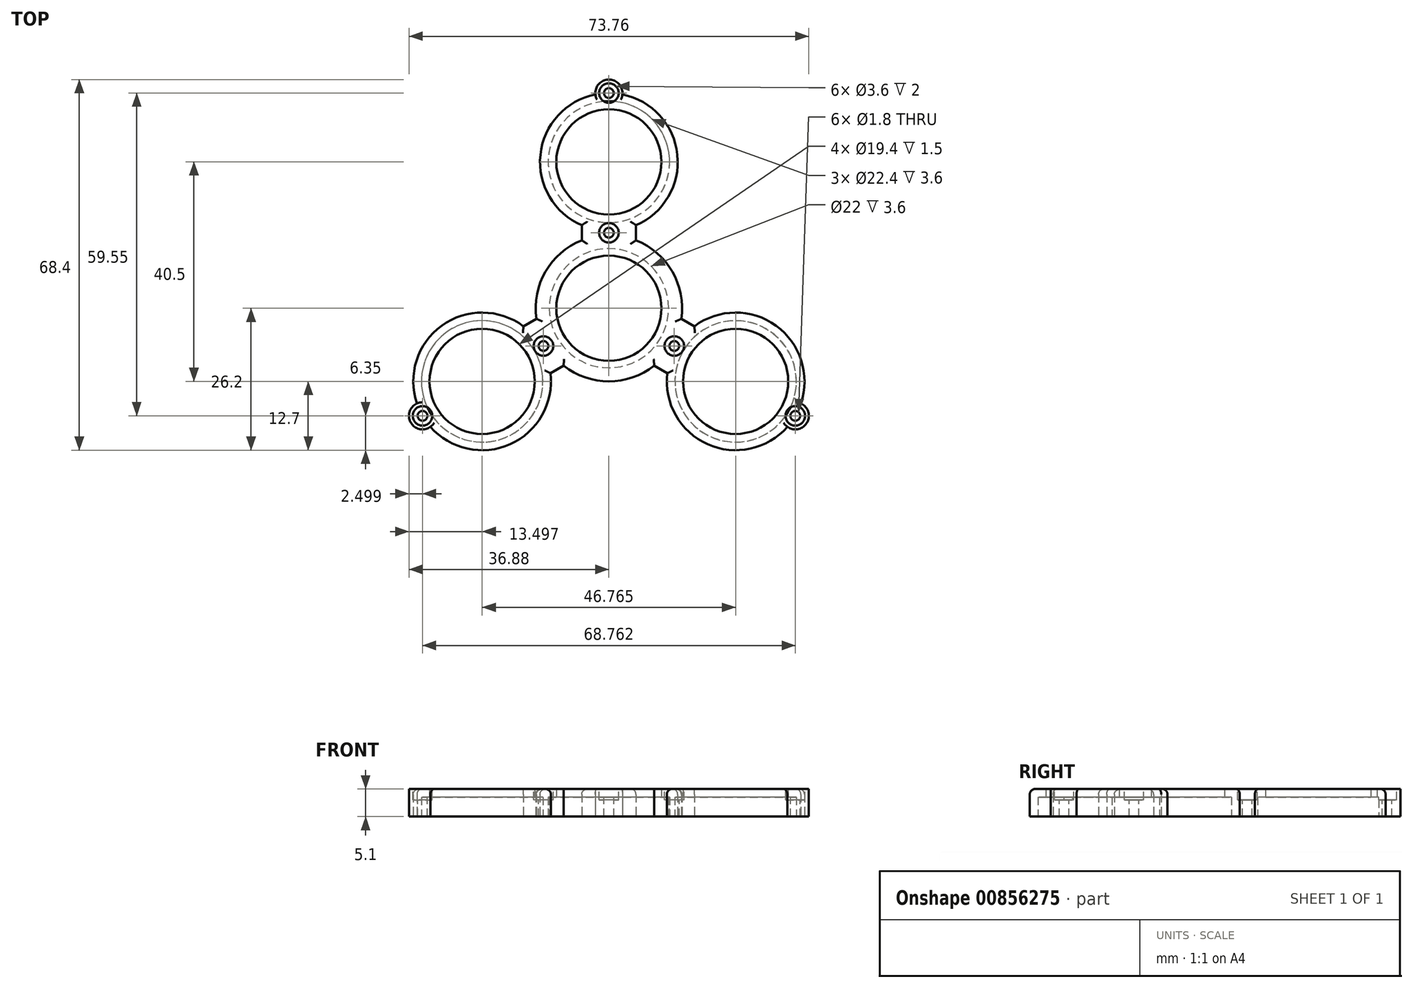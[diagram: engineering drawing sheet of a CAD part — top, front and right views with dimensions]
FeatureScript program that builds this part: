
annotation { "Feature Type Name" : "Feature", "Feature Type Description" : "" }
export const myFeature = defineFeature(function(context is Context, id is Id, definition is map)
    precondition{}
    {
        {
            var Q0;
            Q0=qCreatedBy(makeId("Top.planeOp"),FACE);
            var sketch = newSketch(context, id + "F0", { "sketchPlane" : qUnion([Q0])});
            skCircle(sketch, "E0", {"center": v(0, 0) * mm, "radius": 11 * mm});
            skCircle(sketch, "E1", {"center": v(0, 27) * mm, "radius": 11.2 * mm});
            skLineSegment(sketch, "E2", {"start": v(-5, 15.33) * mm, "end": v(-5, 12.54) * mm});
            skLineSegment(sketch, "E3", {"start": v(5, 15.33) * mm, "end": v(5, 12.54) * mm});
            skLineSegment(sketch, "E4", {"start": v(0, 27) * mm, "end": v(0, 13.5) * mm, "construction": true});
            skLineSegment(sketch, "E5", {"start": v(-5, 13.93) * mm, "end": v(0, 13.93) * mm, "construction": true});
            skLineSegment(sketch, "E6", {"start": v(0, 13.5) * mm, "end": v(0, 0) * mm, "construction": true});
            skLineSegment(sketch, "E7", {"start": v(0, 13.93) * mm, "end": v(5, 13.93) * mm, "construction": true});
            skArc(sketch, "E8", {"start": v(-2.49, 39.45) * mm, "mid": v(0, 37.2) * mm, "end": v(2.49, 39.45) * mm, "construction": true});
            skArc(sketch, "E9", {"start": v(2.49, 39.45) * mm, "mid": v(0, 42.2) * mm, "end": v(-2.49, 39.45) * mm});
            skArc(sketch, "E10", {"start": v(-2.49, 39.45) * mm, "mid": v(-12.63, 28.32) * mm, "end": v(-5, 15.33) * mm});
            skArc(sketch, "E11", {"start": v(-5, 15.33) * mm, "mid": v(0, 14.3) * mm, "end": v(5, 15.33) * mm, "construction": true});
            skArc(sketch, "E12", {"start": v(5, 15.33) * mm, "mid": v(12.63, 28.32) * mm, "end": v(2.49, 39.45) * mm});
            skArc(sketch, "E13", {"start": v(-5, 12.54) * mm, "mid": v(0, -13.5) * mm, "end": v(5, 12.54) * mm});
            skArc(sketch, "E14", {"start": v(5, 12.54) * mm, "mid": v(0, 13.5) * mm, "end": v(-5, 12.54) * mm, "construction": true});
            skArc(sketch, "E15.1.0", {"start": v(-35.41, -17.57) * mm, "mid": v(-36.55, -21.1) * mm, "end": v(-32.92, -21.88) * mm});
            skArc(sketch, "E15.1.1", {"start": v(-32.92, -21.88) * mm, "mid": v(-18.2, -25.1) * mm, "end": v(-10.77, -12) * mm});
            skLineSegment(sketch, "E15.1.2", {"start": v(-10.77, -12) * mm, "end": v(-8.36, -10.6) * mm});
            skArc(sketch, "E15.1.3", {"start": v(-15.77, -3.33) * mm, "mid": v(-30.84, -3.22) * mm, "end": v(-35.41, -17.57) * mm});
            skLineSegment(sketch, "E15.1.4", {"start": v(-15.77, -3.33) * mm, "end": v(-13.36, -1.94) * mm});
            skCircle(sketch, "E15.1.5", {"center": v(-23.38, -13.5) * mm, "radius": 11.2 * mm});
            skArc(sketch, "E15.2.0", {"start": v(32.92, -21.88) * mm, "mid": v(36.55, -21.1) * mm, "end": v(35.41, -17.57) * mm});
            skArc(sketch, "E15.2.1", {"start": v(35.41, -17.57) * mm, "mid": v(30.84, -3.22) * mm, "end": v(15.77, -3.33) * mm});
            skLineSegment(sketch, "E15.2.2", {"start": v(15.77, -3.33) * mm, "end": v(13.36, -1.94) * mm});
            skArc(sketch, "E15.2.3", {"start": v(10.77, -12) * mm, "mid": v(18.2, -25.1) * mm, "end": v(32.92, -21.88) * mm});
            skLineSegment(sketch, "E15.2.4", {"start": v(10.77, -12) * mm, "end": v(8.36, -10.6) * mm});
            skCircle(sketch, "E15.2.5", {"center": v(23.38, -13.5) * mm, "radius": 11.2 * mm});
            skSolve(sketch);
        }
        {
            var Q0;
            Q0=makeQuery(id+"F0.imprint","IMPRINT",FACE,{"disambiguationData":[TD([[makeQuery(id+"F0.imprint","IMPRINT",EDGE,{"derivedFrom":sQuery(id+"F0.wireOp",EDGE,"E0")}),-1.0]])]});
            var Q1;
            Q1=makeQuery(id+"F0.imprint","IMPRINT",FACE,{"disambiguationData":[TD([[makeQuery(id+"F0.imprint","IMPRINT",EDGE,{"derivedFrom":sQuery(id+"F0.wireOp",EDGE,"E15.1.0")}),1.0]])]});
            var Q2;
            Q2=makeQuery(id+"F0.imprint","IMPRINT",FACE,{"disambiguationData":[TD([[makeQuery(id+"F0.imprint","IMPRINT",EDGE,{"derivedFrom":sQuery(id+"F0.wireOp",EDGE,"E15.2.0")}),1.0]])]});
            extrude(context, id + "F1", {"entities" : qUnion([Q0, Q1, Q2]), "depth" : 3.6 * mm, "offsetDistance" : 25 * mm});
        }
        {
            var Q0;
            Q0=makeQuery(id+"F1.opExtrude","CAP_FACE",FACE,{"disambiguationData":[OSD([sQuery(id+"F0.wireOp",EDGE,"E0"),sQuery(id+"F0.wireOp",EDGE,"E1"),sQuery(id+"F0.wireOp",EDGE,"E2"),sQuery(id+"F0.wireOp",EDGE,"E3"),sQuery(id+"F0.wireOp",EDGE,"E9"),sQuery(id+"F0.wireOp",EDGE,"E10"),sQuery(id+"F0.wireOp",EDGE,"E12"),sQuery(id+"F0.wireOp",EDGE,"E13"),sQuery(id+"F0.wireOp",EDGE,"E15.1.0"),sQuery(id+"F0.wireOp",EDGE,"E15.1.1"),sQuery(id+"F0.wireOp",EDGE,"E15.1.2"),sQuery(id+"F0.wireOp",EDGE,"E15.1.3"),sQuery(id+"F0.wireOp",EDGE,"E15.1.4"),sQuery(id+"F0.wireOp",EDGE,"E15.1.5"),sQuery(id+"F0.wireOp",EDGE,"E15.2.0"),sQuery(id+"F0.wireOp",EDGE,"E15.2.1"),sQuery(id+"F0.wireOp",EDGE,"E15.2.2"),sQuery(id+"F0.wireOp",EDGE,"E15.2.3"),sQuery(id+"F0.wireOp",EDGE,"E15.2.4"),sQuery(id+"F0.wireOp",EDGE,"E15.2.5")])],"isStart":false});
            var sketch = newSketch(context, id + "F2", { "sketchPlane" : qUnion([Q0])});
            skCircle(sketch, "E16", {"center": v(0, 0) * mm, "radius": 9.7 * mm});
            skCircle(sketch, "E17", {"center": v(0, 27) * mm, "radius": 9.7 * mm});
            skCircle(sketch, "E18.1.0", {"center": v(-23.38, -13.5) * mm, "radius": 9.7 * mm});
            skCircle(sketch, "E18.2.0", {"center": v(23.38, -13.5) * mm, "radius": 9.7 * mm});
            skSolve(sketch);
        }
        {
            var Q0;
            Q0=makeQuery(id+"F2.imprint","IMPRINT",FACE,{"disambiguationData":[TD([[makeQuery(id+"F2.imprint","IMPRINT",EDGE,{"derivedFrom":sQuery(id+"F2.wireOp",EDGE,"E17")}),-1.0]])]});
            var Q1;
            Q1=makeQuery(id+"F2.imprint","IMPRINT",FACE,{"disambiguationData":[TD([[makeQuery(id+"F2.imprint","IMPRINT",EDGE,{"derivedFrom":makeQuery(id+"F1.opExtrude","CAP_EDGE",EDGE,{"disambiguationData":[OSD([sQuery(id+"F0.wireOp",EDGE,"E0")])],"isStart":false})}),-1.0]])]});
            var Q2;
            Q2=makeQuery(id+"F2.imprint","IMPRINT",FACE,{"disambiguationData":[TD([[makeQuery(id+"F2.imprint","IMPRINT",EDGE,{"derivedFrom":sQuery(id+"F2.wireOp",EDGE,"E18.1.0")}),-1.0]])]});
            var Q3;
            Q3=makeQuery(id+"F2.imprint","IMPRINT",FACE,{"disambiguationData":[TD([[makeQuery(id+"F2.imprint","IMPRINT",EDGE,{"derivedFrom":sQuery(id+"F2.wireOp",EDGE,"E18.2.0")}),-1.0]])]});
            var Q4;
            Q4=makeQuery(id+"F2.imprint","IMPRINT",FACE,{"disambiguationData":[TD([[makeQuery(id+"F2.imprint","IMPRINT",EDGE,{"derivedFrom":sQuery(id+"F2.wireOp",EDGE,"E16")}),-1.0]])]});
            extrude(context, id + "F3", {"entities" : qUnion([Q0, Q1, Q2, Q3, Q4]), "operationType" : NewBodyOperationType.ADD, "depth" : 1.5 * mm, "offsetDistance" : 25 * mm});
        }
        {
            var Q0;
            Q0=makeQuery(id+"F3.opExtrude","CAP_FACE",FACE,{"disambiguationData":[OSD([sQuery(id+"F0.wireOp",EDGE,"E0"),sQuery(id+"F0.wireOp",EDGE,"E2"),sQuery(id+"F0.wireOp",EDGE,"E3"),sQuery(id+"F0.wireOp",EDGE,"E9"),sQuery(id+"F0.wireOp",EDGE,"E10"),sQuery(id+"F0.wireOp",EDGE,"E12"),sQuery(id+"F0.wireOp",EDGE,"E13"),sQuery(id+"F0.wireOp",EDGE,"E15.1.0"),sQuery(id+"F0.wireOp",EDGE,"E15.1.1"),sQuery(id+"F0.wireOp",EDGE,"E15.1.2"),sQuery(id+"F0.wireOp",EDGE,"E15.1.3"),sQuery(id+"F0.wireOp",EDGE,"E15.1.4"),sQuery(id+"F0.wireOp",EDGE,"E15.2.0"),sQuery(id+"F0.wireOp",EDGE,"E15.2.1"),sQuery(id+"F0.wireOp",EDGE,"E15.2.2"),sQuery(id+"F0.wireOp",EDGE,"E15.2.3"),sQuery(id+"F0.wireOp",EDGE,"E15.2.4"),sQuery(id+"F2.wireOp",EDGE,"E17"),sQuery(id+"F2.wireOp",EDGE,"E18.1.0"),sQuery(id+"F2.wireOp",EDGE,"E18.2.0")])],"isStart":false});
            var sketch = newSketch(context, id + "F4", { "sketchPlane" : qUnion([Q0])});
            skCircle(sketch, "E19", {"center": v(0, 39.7) * mm, "radius": 1.8 * mm});
            skCircle(sketch, "E20", {"center": v(0, 13.93) * mm, "radius": 1.8 * mm});
            skPoint(sketch, "E20.centerSnap0", {"position": v(-5, 13.93) * mm});
            skCircle(sketch, "E21.1.0", {"center": v(-34.38, -19.85) * mm, "radius": 1.8 * mm});
            skCircle(sketch, "E21.1.1", {"center": v(-12.07, -6.97) * mm, "radius": 1.8 * mm});
            skCircle(sketch, "E21.2.0", {"center": v(34.38, -19.85) * mm, "radius": 1.8 * mm});
            skCircle(sketch, "E21.2.1", {"center": v(12.07, -6.97) * mm, "radius": 1.8 * mm});
            skPoint(sketch, "E21.center", {"position": v(0, 0) * mm});
            skSolve(sketch);
        }
        {
            var Q0;
            Q0=makeQuery(id+"F4.imprint","IMPRINT",FACE,{"disambiguationData":[TD([[makeQuery(id+"F4.imprint","IMPRINT",EDGE,{"derivedFrom":sQuery(id+"F4.wireOp",EDGE,"E19")}),1.0]])]});
            var Q1;
            Q1=makeQuery(id+"F4.imprint","IMPRINT",FACE,{"disambiguationData":[TD([[makeQuery(id+"F4.imprint","IMPRINT",EDGE,{"derivedFrom":sQuery(id+"F4.wireOp",EDGE,"E20")}),1.0]])]});
            var Q2;
            Q2=makeQuery(id+"F4.imprint","IMPRINT",FACE,{"disambiguationData":[TD([[makeQuery(id+"F4.imprint","IMPRINT",EDGE,{"derivedFrom":sQuery(id+"F4.wireOp",EDGE,"E21.1.1")}),1.0]])]});
            var Q3;
            Q3=makeQuery(id+"F4.imprint","IMPRINT",FACE,{"disambiguationData":[TD([[makeQuery(id+"F4.imprint","IMPRINT",EDGE,{"derivedFrom":sQuery(id+"F4.wireOp",EDGE,"E21.1.0")}),1.0]])]});
            var Q4;
            Q4=makeQuery(id+"F4.imprint","IMPRINT",FACE,{"disambiguationData":[TD([[makeQuery(id+"F4.imprint","IMPRINT",EDGE,{"derivedFrom":sQuery(id+"F4.wireOp",EDGE,"E21.2.1")}),1.0]])]});
            var Q5;
            Q5=makeQuery(id+"F4.imprint","IMPRINT",FACE,{"disambiguationData":[TD([[makeQuery(id+"F4.imprint","IMPRINT",EDGE,{"derivedFrom":sQuery(id+"F4.wireOp",EDGE,"E21.2.0")}),1.0]])]});
            extrude(context, id + "F5", {"entities" : qUnion([Q0, Q1, Q2, Q3, Q4, Q5]), "operationType" : NewBodyOperationType.REMOVE, "oppositeDirection" : true, "depth" : 2 * mm, "offsetDistance" : 25 * mm});
        }
        {
            var Q0;
            Q0=makeQuery(id+"F3.opExtrude","CAP_FACE",FACE,{"disambiguationData":[OSD([sQuery(id+"F0.wireOp",EDGE,"E2"),sQuery(id+"F0.wireOp",EDGE,"E3"),sQuery(id+"F0.wireOp",EDGE,"E9"),sQuery(id+"F0.wireOp",EDGE,"E10"),sQuery(id+"F0.wireOp",EDGE,"E12"),sQuery(id+"F0.wireOp",EDGE,"E13"),sQuery(id+"F0.wireOp",EDGE,"E15.1.0"),sQuery(id+"F0.wireOp",EDGE,"E15.1.1"),sQuery(id+"F0.wireOp",EDGE,"E15.1.2"),sQuery(id+"F0.wireOp",EDGE,"E15.1.3"),sQuery(id+"F0.wireOp",EDGE,"E15.1.4"),sQuery(id+"F0.wireOp",EDGE,"E15.2.0"),sQuery(id+"F0.wireOp",EDGE,"E15.2.1"),sQuery(id+"F0.wireOp",EDGE,"E15.2.2"),sQuery(id+"F0.wireOp",EDGE,"E15.2.3"),sQuery(id+"F0.wireOp",EDGE,"E15.2.4"),sQuery(id+"F2.wireOp",EDGE,"E16"),sQuery(id+"F2.wireOp",EDGE,"E17"),sQuery(id+"F2.wireOp",EDGE,"E18.1.0"),sQuery(id+"F2.wireOp",EDGE,"E18.2.0")])],"isStart":false});
            var sketch = newSketch(context, id + "F6", { "sketchPlane" : qUnion([Q0])});
            skCircle(sketch, "E22", {"center": v(0, 39.7) * mm, "radius": 0.9 * mm});
            skCircle(sketch, "E23", {"center": v(0, 13.93) * mm, "radius": 0.9 * mm});
            skCircle(sketch, "E24.1.0", {"center": v(-34.38, -19.85) * mm, "radius": 0.9 * mm});
            skCircle(sketch, "E24.1.1", {"center": v(-12.07, -6.97) * mm, "radius": 0.9 * mm});
            skCircle(sketch, "E24.2.0", {"center": v(34.38, -19.85) * mm, "radius": 0.9 * mm});
            skCircle(sketch, "E24.2.1", {"center": v(12.07, -6.97) * mm, "radius": 0.9 * mm});
            skPoint(sketch, "E24.center", {"position": v(0, 0) * mm});
            skSolve(sketch);
        }
        {
            var Q0;
            Q0=makeQuery(id+"F6.imprint","IMPRINT",FACE,{"disambiguationData":[TD([[makeQuery(id+"F6.imprint","IMPRINT",EDGE,{"derivedFrom":sQuery(id+"F6.wireOp",EDGE,"E22")}),1.0]])]});
            var Q1;
            Q1=makeQuery(id+"F6.imprint","IMPRINT",FACE,{"disambiguationData":[TD([[makeQuery(id+"F6.imprint","IMPRINT",EDGE,{"derivedFrom":sQuery(id+"F6.wireOp",EDGE,"E23")}),1.0]])]});
            var Q2;
            Q2=makeQuery(id+"F6.imprint","IMPRINT",FACE,{"disambiguationData":[TD([[makeQuery(id+"F6.imprint","IMPRINT",EDGE,{"derivedFrom":sQuery(id+"F6.wireOp",EDGE,"E24.1.1")}),1.0]])]});
            var Q3;
            Q3=makeQuery(id+"F6.imprint","IMPRINT",FACE,{"disambiguationData":[TD([[makeQuery(id+"F6.imprint","IMPRINT",EDGE,{"derivedFrom":sQuery(id+"F6.wireOp",EDGE,"E24.1.0")}),1.0]])]});
            var Q4;
            Q4=makeQuery(id+"F6.imprint","IMPRINT",FACE,{"disambiguationData":[TD([[makeQuery(id+"F6.imprint","IMPRINT",EDGE,{"derivedFrom":sQuery(id+"F6.wireOp",EDGE,"E24.2.1")}),1.0]])]});
            var Q5;
            Q5=makeQuery(id+"F6.imprint","IMPRINT",FACE,{"disambiguationData":[TD([[makeQuery(id+"F6.imprint","IMPRINT",EDGE,{"derivedFrom":sQuery(id+"F6.wireOp",EDGE,"E24.2.0")}),1.0]])]});
            var Q6;
            Q6=makeQuery(id+"F1.opExtrude","CAP_FACE",FACE,{"disambiguationData":[OSD([sQuery(id+"F0.wireOp",EDGE,"E0"),sQuery(id+"F0.wireOp",EDGE,"E1"),sQuery(id+"F0.wireOp",EDGE,"E2"),sQuery(id+"F0.wireOp",EDGE,"E3"),sQuery(id+"F0.wireOp",EDGE,"E9"),sQuery(id+"F0.wireOp",EDGE,"E10"),sQuery(id+"F0.wireOp",EDGE,"E12"),sQuery(id+"F0.wireOp",EDGE,"E13"),sQuery(id+"F0.wireOp",EDGE,"E15.1.0"),sQuery(id+"F0.wireOp",EDGE,"E15.1.1"),sQuery(id+"F0.wireOp",EDGE,"E15.1.2"),sQuery(id+"F0.wireOp",EDGE,"E15.1.3"),sQuery(id+"F0.wireOp",EDGE,"E15.1.4"),sQuery(id+"F0.wireOp",EDGE,"E15.1.5"),sQuery(id+"F0.wireOp",EDGE,"E15.2.0"),sQuery(id+"F0.wireOp",EDGE,"E15.2.1"),sQuery(id+"F0.wireOp",EDGE,"E15.2.2"),sQuery(id+"F0.wireOp",EDGE,"E15.2.3"),sQuery(id+"F0.wireOp",EDGE,"E15.2.4"),sQuery(id+"F0.wireOp",EDGE,"E15.2.5")])],"isStart":true});
            extrude(context, id + "F7", {"entities" : qUnion([Q0, Q1, Q2, Q3, Q4, Q5]), "operationType" : NewBodyOperationType.REMOVE, "endBound" : BoundingType.UP_TO_SURFACE, "oppositeDirection" : true, "depth" : 25 * mm, "endBoundEntityFace" : qUnion([Q6]), "offsetDistance" : 25 * mm});
        }
        {
            var Q0;
            Q0=makeQuery(id+"F3.opExtrude","CAP_EDGE",EDGE,{"disambiguationData":[OSD([sQuery(id+"F0.wireOp",EDGE,"E15.1.1")])],"isStart":false});
            var Q1;
            Q1=makeQuery(id+"F3.opExtrude","CAP_EDGE",EDGE,{"disambiguationData":[OSD([sQuery(id+"F0.wireOp",EDGE,"E15.1.2")])],"isStart":false});
            var Q2;
            {var subQ0=sQuery(id+"F0.wireOp",EDGE,"E13");Q2=makeQuery(id+"F3.opExtrude","CAP_EDGE",EDGE,{"disambiguationData":[OSD([subQ0]),TDD([makeQuery(id+"F2.imprint","IMPRINT",EDGE,{"derivedFrom":makeQuery(id+"F1.opExtrude","CAP_EDGE",EDGE,{"disambiguationData":[OSD([subQ0]),TDD([makeQuery(id+"F0.imprint","IMPRINT",EDGE,{"disambiguationData":[TD([[makeQuery(id+"F0.imprint","INTERSECT",VERTEX,{"derivedFrom":[subQ0,sQuery(id+"F0.wireOp",EDGE,"E15.1.2")]}),-1.0]])],"derivedFrom":subQ0})])],"isStart":false})})])],"isStart":false});}
            var Q3;
            Q3=makeQuery(id+"F3.opExtrude","CAP_EDGE",EDGE,{"disambiguationData":[OSD([sQuery(id+"F0.wireOp",EDGE,"E15.2.4")])],"isStart":false});
            var Q4;
            Q4=makeQuery(id+"F3.opExtrude","CAP_EDGE",EDGE,{"disambiguationData":[OSD([sQuery(id+"F0.wireOp",EDGE,"E15.2.3")])],"isStart":false});
            var Q5;
            Q5=makeQuery(id+"F3.opExtrude","CAP_EDGE",EDGE,{"disambiguationData":[OSD([sQuery(id+"F0.wireOp",EDGE,"E15.2.1")])],"isStart":false});
            var Q6;
            Q6=makeQuery(id+"F3.opExtrude","CAP_EDGE",EDGE,{"disambiguationData":[OSD([sQuery(id+"F0.wireOp",EDGE,"E15.2.2")])],"isStart":false});
            var Q7;
            {var subQ0=sQuery(id+"F0.wireOp",EDGE,"E13");Q7=makeQuery(id+"F3.opExtrude","CAP_EDGE",EDGE,{"disambiguationData":[OSD([subQ0]),TDD([makeQuery(id+"F2.imprint","IMPRINT",EDGE,{"derivedFrom":makeQuery(id+"F1.opExtrude","CAP_EDGE",EDGE,{"disambiguationData":[OSD([subQ0]),TDD([makeQuery(id+"F0.imprint","IMPRINT",EDGE,{"disambiguationData":[TD([[makeQuery(id+"F0.imprint","INTERSECT",VERTEX,{"derivedFrom":[sQuery(id+"F0.wireOp",EDGE,"E3"),subQ0]}),1.0]])],"derivedFrom":subQ0})])],"isStart":false})})])],"isStart":false});}
            var Q8;
            Q8=makeQuery(id+"F3.opExtrude","CAP_EDGE",EDGE,{"disambiguationData":[OSD([sQuery(id+"F0.wireOp",EDGE,"E3")])],"isStart":false});
            var Q9;
            Q9=makeQuery(id+"F3.opExtrude","CAP_EDGE",EDGE,{"disambiguationData":[OSD([sQuery(id+"F0.wireOp",EDGE,"E12")])],"isStart":false});
            var Q10;
            Q10=makeQuery(id+"F3.opExtrude","CAP_EDGE",EDGE,{"disambiguationData":[OSD([sQuery(id+"F0.wireOp",EDGE,"E10")])],"isStart":false});
            var Q11;
            Q11=makeQuery(id+"F3.opExtrude","CAP_EDGE",EDGE,{"disambiguationData":[OSD([sQuery(id+"F0.wireOp",EDGE,"E2")])],"isStart":false});
            var Q12;
            {var subQ0=sQuery(id+"F0.wireOp",EDGE,"E13");Q12=makeQuery(id+"F3.opExtrude","CAP_EDGE",EDGE,{"disambiguationData":[OSD([subQ0]),TDD([makeQuery(id+"F2.imprint","IMPRINT",EDGE,{"derivedFrom":makeQuery(id+"F1.opExtrude","CAP_EDGE",EDGE,{"disambiguationData":[OSD([subQ0]),TDD([makeQuery(id+"F0.imprint","IMPRINT",EDGE,{"disambiguationData":[TD([[makeQuery(id+"F0.imprint","INTERSECT",VERTEX,{"derivedFrom":[sQuery(id+"F0.wireOp",EDGE,"E2"),subQ0]}),-1.0]])],"derivedFrom":subQ0})])],"isStart":false})})])],"isStart":false});}
            var Q13;
            Q13=makeQuery(id+"F3.opExtrude","CAP_EDGE",EDGE,{"disambiguationData":[OSD([sQuery(id+"F0.wireOp",EDGE,"E15.1.4")])],"isStart":false});
            var Q14;
            Q14=makeQuery(id+"F3.opExtrude","CAP_EDGE",EDGE,{"disambiguationData":[OSD([sQuery(id+"F0.wireOp",EDGE,"E15.1.3")])],"isStart":false});
            fillet(context, id + "F8", {"entities" : qUnion([Q0, Q1, Q2, Q3, Q4, Q5, Q6, Q7, Q8, Q9, Q10, Q11, Q12, Q13, Q14]), "radius" : 1 * mm, "tangentPropagation" : true, "allowEdgeOverflow" : false});
        }
    });
